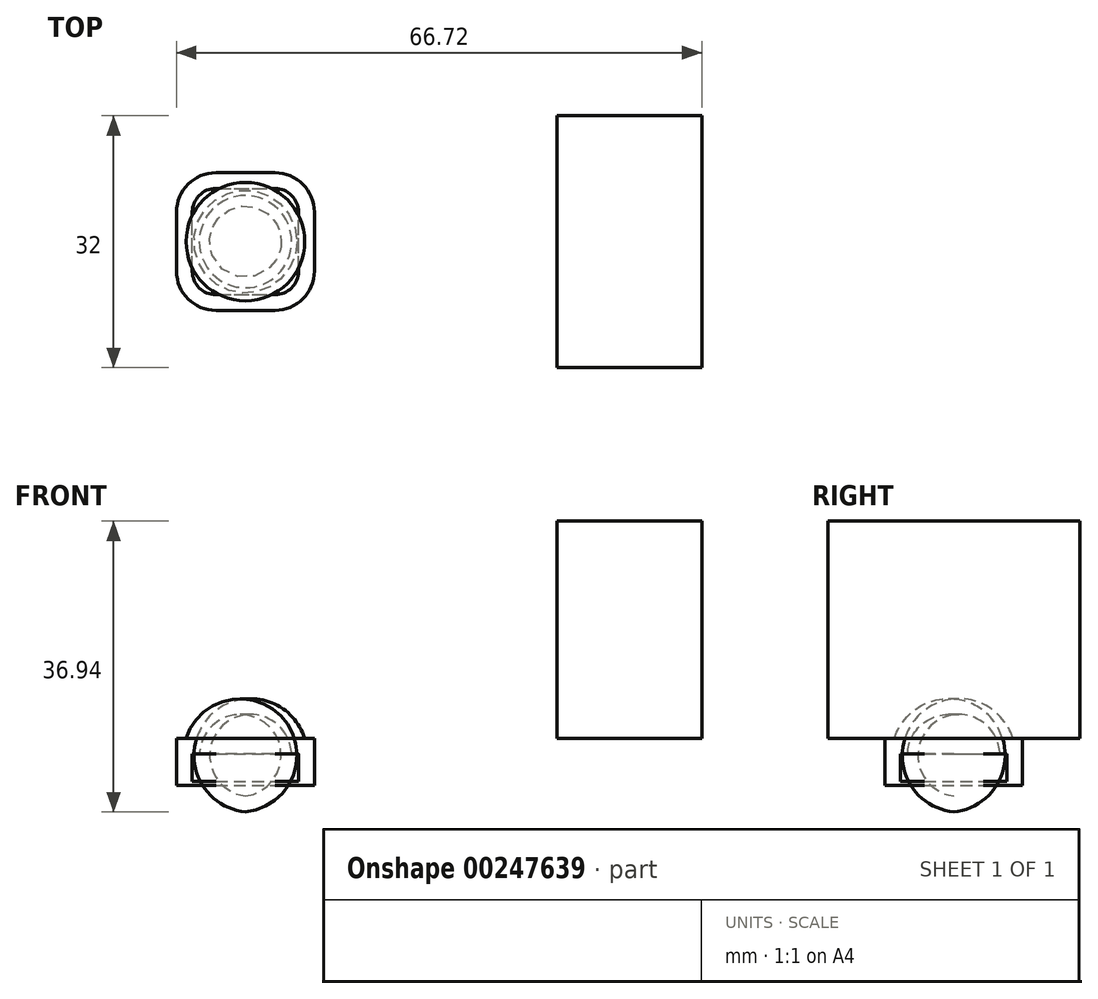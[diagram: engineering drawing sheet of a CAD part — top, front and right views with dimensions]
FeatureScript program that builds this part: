
annotation { "Feature Type Name" : "Feature", "Feature Type Description" : "" }
export const myFeature = defineFeature(function(context is Context, id is Id, definition is map)
    precondition{}
    {
        {
            var Q0;
            Q0=qCreatedBy(makeId("Top.planeOp"),FACE);
            var sketch = newSketch(context, id + "F0", { "sketchPlane" : qUnion([Q0])});
            skLineSegment(sketch, "E0.bottom", {"start": v(9.2, -16) * mm, "end": v(-9.2, -16) * mm});
            skLineSegment(sketch, "E0.top", {"start": v(9.2, 16) * mm, "end": v(-9.2, 16) * mm});
            skLineSegment(sketch, "E0.left", {"start": v(9.2, -16) * mm, "end": v(9.2, 16) * mm});
            skLineSegment(sketch, "E0.right", {"start": v(-9.2, -16) * mm, "end": v(-9.2, 16) * mm});
            skPoint(sketch, "E0.middle", {"position": v(0, 0) * mm});
            skSolve(sketch);
        }
        {
            var Q0;
            Q0=makeQuery(id+"F0.imprint","IMPRINT",FACE,{"disambiguationData":[TD([[makeQuery(id+"F0.imprint","IMPRINT",EDGE,{"derivedFrom":sQuery(id+"F0.wireOp",EDGE,"E0.bottom")}),-1.0]])]});
            extrude(context, id + "F1", {"entities" : qUnion([Q0]), "depth" : 27.6 * mm});
        }
        {
            var Q0;
            Q0=qCreatedBy(makeId("Front.planeOp"),FACE);
            var sketch = newSketch(context, id + "F2", { "sketchPlane" : qUnion([Q0])});
            skLineSegment(sketch, "E1", {"start": v(-57.52, 0) * mm, "end": v(-40.02, 0) * mm});
            skLineSegment(sketch, "E2", {"start": v(-48.77, 0) * mm, "end": v(-48.77, 5) * mm});
            skLineSegment(sketch, "E3", {"start": v(-57.52, 0) * mm, "end": v(-57.52, -6) * mm});
            skLineSegment(sketch, "E4", {"start": v(-57.52, -6) * mm, "end": v(-40.02, -6) * mm});
            skLineSegment(sketch, "E5", {"start": v(-40.02, -6) * mm, "end": v(-40.02, 0) * mm});
            skLineSegment(sketch, "E6", {"start": v(-48.77, 0) * mm, "end": v(-44.4, 0) * mm});
            skLineSegment(sketch, "E7.MirrorCS", {"start": v(-48.77, 0) * mm, "end": v(-53.14, 0) * mm});
            skArc(sketch, "E8", {"start": v(-41.24, 0) * mm, "mid": v(-44.12, 3.83) * mm, "end": v(-48.77, 5) * mm});
            skSolve(sketch);
        }
        {
            var Q0;
            {var subQ0=sQuery(id+"F2.wireOp",EDGE,"E3");Q0=makeQuery(id+"F2.imprint","IMPRINT",FACE,{"disambiguationData":[TD([[makeQuery(id+"F2.imprint","IMPRINT",EDGE,{"derivedFrom":subQ0}),1.0]])]});}
            extrude(context, id + "F3", {"entities" : qUnion([Q0]), "depth" : 17.5 * mm, "symmetric" : true});
        }
        {
            var Q0;
            Q0=makeQuery(id+"F2.imprint","IMPRINT",FACE,{"disambiguationData":[TD([[makeQuery(id+"F2.imprint","IMPRINT",EDGE,{"derivedFrom":sQuery(id+"F2.wireOp",EDGE,"E2")}),-1.0]])]});
            var Q1;
            Q1=sQuery(id+"F2.wireOp",EDGE,"E2");
            revolve(context, id + "F4", {"operationType" : NewBodyOperationType.ADD, "entities" : qUnion([Q0]), "axis" : qUnion([Q1]), "revolveType" : RevolveType.FULL});
        }
        {
            var Q0;
            Q0=makeQuery(id+"F3.opExtrude","CAP_EDGE",EDGE,{"disambiguationData":[OSD([sQuery(id+"F2.wireOp",EDGE,"E5")])],"isStart":true});
            var Q1;
            Q1=makeQuery(id+"F3.opExtrude","CAP_EDGE",EDGE,{"disambiguationData":[OSD([sQuery(id+"F2.wireOp",EDGE,"E5")])],"isStart":false});
            var Q2;
            Q2=makeQuery(id+"F3.opExtrude","CAP_EDGE",EDGE,{"disambiguationData":[OSD([sQuery(id+"F2.wireOp",EDGE,"E3")])],"isStart":false});
            var Q3;
            Q3=makeQuery(id+"F3.opExtrude","CAP_EDGE",EDGE,{"disambiguationData":[OSD([sQuery(id+"F2.wireOp",EDGE,"E3")])],"isStart":true});
            fillet(context, id + "F5", {"entities" : qUnion([Q0, Q1, Q2, Q3]), "radius" : 5 * mm, "tangentPropagation" : true, "allowEdgeOverflow" : false});
        }
        {
            var Q0;
            Q0=makeQuery(id+"F3.opExtrude","SWEPT_FACE",FACE,{"disambiguationData":[OSD([sQuery(id+"F2.wireOp",EDGE,"E4")])]});
            shell(context, id + "F6", {"entities" : qUnion([Q0]), "thickness" : 2 * mm});
        }
        {
            var Q0;
            Q0=makeQuery(id+"F3.opExtrude","SWEPT_FACE",FACE,{"disambiguationData":[OSD([sQuery(id+"F2.wireOp",EDGE,"E4")])]});
            var sketch = newSketch(context, id + "F7", { "sketchPlane" : qUnion([Q0])});
            skLineSegment(sketch, "E9.0", {"start": v(-55.52, 3.75) * mm, "end": v(-55.52, -3.75) * mm});
            skArc(sketch, "E10.0", {"start": v(-55.52, -3.75) * mm, "mid": v(-54.64, -5.87) * mm, "end": v(-52.52, -6.75) * mm});
            skLineSegment(sketch, "E11.0", {"start": v(-52.52, -6.75) * mm, "end": v(-45.02, -6.75) * mm});
            skArc(sketch, "E12.0", {"start": v(-52.52, 6.75) * mm, "mid": v(-54.64, 5.87) * mm, "end": v(-55.52, 3.75) * mm});
            skLineSegment(sketch, "E13.0", {"start": v(-52.52, 6.75) * mm, "end": v(-45.02, 6.75) * mm});
            skArc(sketch, "E14.0", {"start": v(-42.02, 3.75) * mm, "mid": v(-42.9, 5.87) * mm, "end": v(-45.02, 6.75) * mm});
            skLineSegment(sketch, "E15.0", {"start": v(-42.02, 3.75) * mm, "end": v(-42.02, -3.75) * mm});
            skArc(sketch, "E16.0", {"start": v(-45.02, -6.75) * mm, "mid": v(-42.9, -5.87) * mm, "end": v(-42.02, -3.75) * mm});
            skSolve(sketch);
        }
        {
            var Q0;
            Q0=makeQuery(id+"F7.imprint","IMPRINT",FACE,{"disambiguationData":[TD([[makeQuery(id+"F7.imprint","IMPRINT",EDGE,{"derivedFrom":sQuery(id+"F7.wireOp",EDGE,"E9.0")}),1.0]])]});
            extrude(context, id + "F8", {"entities" : qUnion([Q0]), "operationType" : NewBodyOperationType.ADD, "depth" : -.5 * mm});
        }
    });
